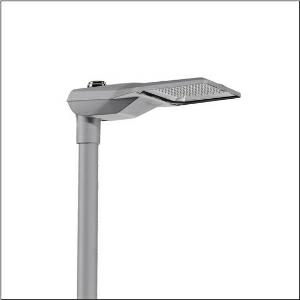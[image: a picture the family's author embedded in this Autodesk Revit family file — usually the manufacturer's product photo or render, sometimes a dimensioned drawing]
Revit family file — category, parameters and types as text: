
# Revit family: streetlight_sl_21_midi___st0_5a_5xe7b47n08mb_0aeb
name_source: partatom
category: Lighting Fixtures
units: mm (PartAtom-declared; Revit-internal decimal feet)

## family parameters
Cut with Voids When Loaded = No
Host = Face
Light Source = No
Part Type = Normal
Room Calculation Point = No
Round Connector Dimension = Use Diameter
Shared = No

## types (1)
- --- (1 x LED, 20180 lm, 147 W, 4000K)
    Apparent Load = 147 VA
    CIE Flux Codes = 41 75 97 100 100
    Color Rendering = 70
    Color Temperature = 4000K
    Default Elevation = 1800 mm
    Description = Streetlight SL 21 midi, mast luminaire, primary light control with lens, of PMMA, primary optical cover: cover, of toughened safety glass, transparent, light distribution: ST0.5a, light emission: direct distribution, primary light characteristic: asymmetric, installation type: side-entry, LED, 3G 2.5mm², High Power LED, rated luminous flux: 20.180lm, luminous efficacy: 137lm/W, light colour: 740, colour temperature: 4000K, control gear: NEMA (7pin), control: overheat protection, pre-setting: linear dimming characteristic, constant luminous flux control, time-dependent luminous flux control, flexible luminous flux parameterisation, mains connection: 220..240V, AC, 50/60Hz, connection cable pre-assembled, cable length: 12,5m, wiring characteristics: H05VV-F, start of lifetime: 147W, end of service life: 155W, reduction: 65W, luminaire housing, of diecast aluminium (EN AC-44300), powder-coated, Siteco® metallic grey (DB 702S), corrosivity category C5 mid according to DIN EN ISO 12944, multi-level sealing system, sealing non-destructively replaceable, inclination adjustable: 0°, 5°, 10°, 15°, length: 644mm, width: 335mm, height: 110mm, spigot size: 42mm (side-entry), mounting height: 4..8m, protection rating (complete): IP66, insulation class (complete): insulation class I (protective earthing), certification: CE, ENEC, ENEC+, VDE, impact resistance: IK09, permissible operating ambient temperature for outdoor applications: -40..+50°C, standard-compliant lighting for roads and squares, packaging unit: 1 piece

Light Distribution: ST0.5a
    Height = 111 mm
    Lamp = 1 x LED
    Lamp Light Flux = 20180 lm
    Lamp Power = 147 W
    Lamp count = 1
    Length = 644 mm
    Luminous efficacy = 137 lm/W
    Manufacturer = Siteco
    ModVariant = No
    Model = 5XE7B47N08MB
    Number of Poles = 1
    OnlyDefault = Yes
    Power Factor = 1
    Product Name = Streetlight SL 21 midi | ST0.5a
    Product group = mast luminaire | pylon top
    ProductGroupID = 6100
    Protection Class = Protection class I
    Protection Degree = IP 66
    RLX_Detail_Level = 1
    RLX_Emergency_Light_Flux = 0 lm
    RLX_Emergency_Type = 0
    RLX_Emergency_Type_DB = No
    RlxData = <blob elided: 101189 chars, md5=4a2f369b>
    Socket = socket
    Standby Power = 0 W
    System Light Flux = 20180 lm
    System Power = 147 W
    Type Comments = factory setting: luminous flux: 100 % | dim-lin: 254 | 750 mA
    Type Image = l_1294377.jpg
    URL = http://relux.com
    VarID = @adj_134692
    Voltage = 0 V
    Weight = 0.00 kg
    Width = 336 mm

## geometry (parser evidence)
native form markers: Blend x4, Sweep x8
no freeform markers — native parametric forms only
